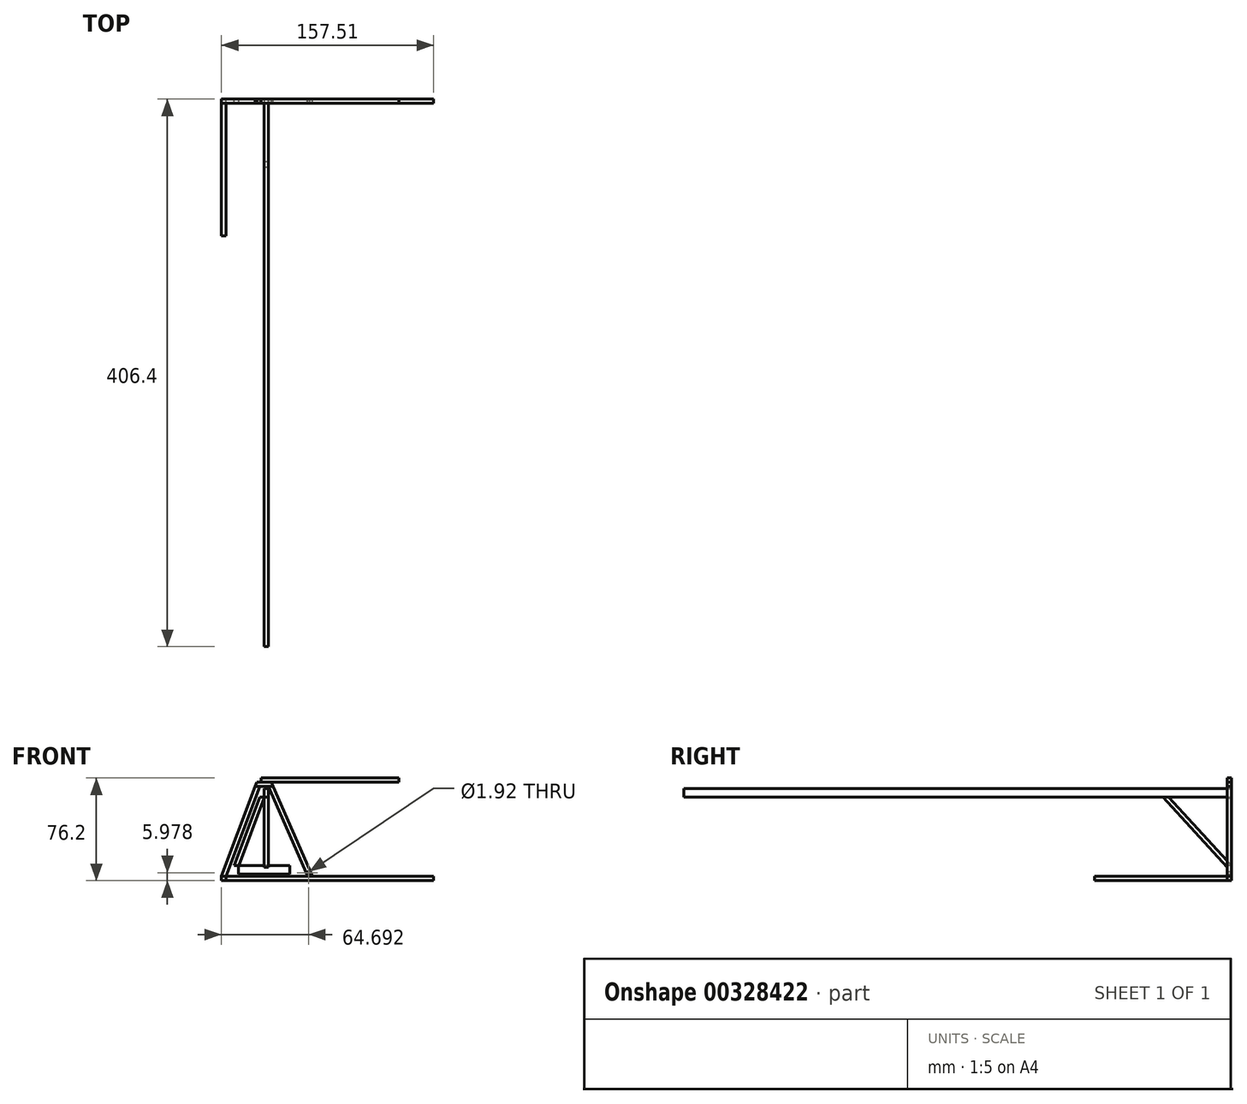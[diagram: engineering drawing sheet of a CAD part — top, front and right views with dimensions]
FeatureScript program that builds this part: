
annotation { "Feature Type Name" : "Feature", "Feature Type Description" : "" }
export const myFeature = defineFeature(function(context is Context, id is Id, definition is map)
    precondition{}
    {
        {
            var Q0;
            Q0=qCreatedBy(makeId("Front.planeOp"),FACE);
            var sketch = newSketch(context, id + "F0", { "sketchPlane" : qUnion([Q0])});
            skLineSegment(sketch, "E0", {"start": v(-19.05, 0) * mm, "end": v(19.05, 0) * mm});
            skLineSegment(sketch, "E1", {"start": v(19.05, 0) * mm, "end": v(19.05, 6.35) * mm});
            skLineSegment(sketch, "E2", {"start": v(19.05, 6.35) * mm, "end": v(-19.05, 6.35) * mm});
            skLineSegment(sketch, "E3", {"start": v(-19.05, 6.35) * mm, "end": v(-19.05, 0) * mm});
            skLineSegment(sketch, "E4", {"start": v(19.05, 6.35) * mm, "end": v(22.23, 6.35) * mm});
            skLineSegment(sketch, "E5", {"start": v(22.23, 6.35) * mm, "end": v(22.23, 0) * mm});
            skLineSegment(sketch, "E6", {"start": v(22.23, 0) * mm, "end": v(19.05, 0) * mm});
            skLineSegment(sketch, "E7", {"start": v(-19.05, 0) * mm, "end": v(-22.23, 0) * mm});
            skLineSegment(sketch, "E8", {"start": v(-22.23, 0) * mm, "end": v(-22.23, 6.35) * mm});
            skLineSegment(sketch, "E9", {"start": v(-22.23, 6.35) * mm, "end": v(-19.05, 6.35) * mm});
            skLineSegment(sketch, "E10", {"start": v(-22.23, 6.35) * mm, "end": v(-3.17, 57.15) * mm});
            skLineSegment(sketch, "E11", {"start": v(-3.18, 57.15) * mm, "end": v(0, 57.15) * mm});
            skLineSegment(sketch, "E12", {"start": v(3.17, 57.15) * mm, "end": v(22.23, 6.35) * mm});
            skLineSegment(sketch, "E13", {"start": v(0, 57.15) * mm, "end": v(3.17, 57.15) * mm});
            skLineSegment(sketch, "E14", {"start": v(-3.18, 57.15) * mm, "end": v(-3.18, 63.5) * mm});
            skLineSegment(sketch, "E15", {"start": v(-3.18, 63.5) * mm, "end": v(0, 63.5) * mm});
            skLineSegment(sketch, "E16", {"start": v(0, 63.5) * mm, "end": v(0, 57.15) * mm});
            skLineSegment(sketch, "E17", {"start": v(3.17, 57.15) * mm, "end": v(3.17, 63.5) * mm});
            skLineSegment(sketch, "E18", {"start": v(0, 63.5) * mm, "end": v(3.17, 63.5) * mm});
            skLineSegment(sketch, "E19", {"start": v(0, 56.57) * mm, "end": v(-18.83, 6.35) * mm});
            skLineSegment(sketch, "E20", {"start": v(0, 57.15) * mm, "end": v(0, 6.35) * mm, "construction": true});
            skLineSegment(sketch, "E21.MirrorCS", {"start": v(0, 56.57) * mm, "end": v(18.83, 6.35) * mm});
            skLineSegment(sketch, "E22", {"start": v(0, 57.15) * mm, "end": v(0, 56.57) * mm});
            skSolve(sketch);
        }
        {
            var Q0;
            Q0=makeQuery(id+"F0.imprint","IMPRINT",FACE,{"disambiguationData":[TD([[makeQuery(id+"F0.imprint","IMPRINT",EDGE,{"derivedFrom":sQuery(id+"F0.wireOp",EDGE,"E13")}),1.0]])]});
            extrude(context, id + "F1", {"entities" : qUnion([Q0]), "depth" : 406.4 * mm});
        }
        {
            var Q0;
            {var subQ1=sQuery(id+"F0.wireOp",EDGE,"E9");Q0=makeQuery(id+"F0.imprint","IMPRINT",FACE,{"disambiguationData":[TD([[makeQuery(id+"F0.imprint","IMPRINT",EDGE,{"derivedFrom":subQ1}),1.0]])]});}
            extrude(context, id + "F2", {"entities" : qUnion([Q0]), "depth" : 3.17 * mm});
        }
        {
            var Q0;
            Q0=makeQuery(id+"F0.imprint","IMPRINT",FACE,{"disambiguationData":[TD([[makeQuery(id+"F0.imprint","IMPRINT",EDGE,{"derivedFrom":sQuery(id+"F0.wireOp",EDGE,"E0")}),1.0]])]});
            extrude(context, id + "F3", {"entities" : qUnion([Q0]), "depth" : 1 / 203.2 * mm});
        }
        {
            var Q0;
            Q0=qCreatedBy(makeId("Right.planeOp"),FACE);
            var sketch = newSketch(context, id + "F4", { "sketchPlane" : qUnion([Q0])});
            skLineSegment(sketch, "E23.0.1", {"start": v(0, 6.35) * mm, "end": v(-3.18, 6.35) * mm});
            skLineSegment(sketch, "E23.0.3", {"start": v(-3.18, 6.35) * mm, "end": v(0, 6.35) * mm});
            skLineSegment(sketch, "E24.0.1", {"start": v(0, 57.15) * mm, "end": v(-406.4, 57.15) * mm});
            skLineSegment(sketch, "E24.0.3", {"start": v(-406.4, 57.15) * mm, "end": v(0, 57.15) * mm});
            skLineSegment(sketch, "E25", {"start": v(0, 6.35) * mm, "end": v(-46.5, 57.15) * mm});
            skLineSegment(sketch, "E26.0", {"start": v(-0.15, 1.81) * mm, "end": v(-50.8, 57.15) * mm});
            skLineSegment(sketch, "E27.0.1", {"start": v(-3.18, 6.35) * mm, "end": v(-3.18, 0) * mm});
            skLineSegment(sketch, "E27.0.3", {"start": v(-3.18, 0) * mm, "end": v(-3.18, 6.35) * mm});
            skSolve(sketch);
        }
        {
            var Q0;
            Q0 = qSketchRegion(id + "F4", true);
            extrude(context, id + "F5", {"entities" : qUnion([Q0]), "depth" : 3.17 * mm});
        }
        {
            var Q0;
            Q0=makeQuery(id+"F3.opExtrude","CAP_FACE",FACE,{"disambiguationData":[OSD([sQuery(id+"F0.wireOp",EDGE,"E0"),sQuery(id+"F0.wireOp",EDGE,"E1"),sQuery(id+"F0.wireOp",EDGE,"E2"),sQuery(id+"F0.wireOp",EDGE,"E3")])],"isStart":true});
            var sketch = newSketch(context, id + "F6", { "sketchPlane" : qUnion([Q0])});
            skLineSegment(sketch, "E28", {"start": v(-3.26, 64.88) * mm, "end": v(-32.43, -1.8) * mm});
            skLineSegment(sketch, "E29", {"start": v(-32.43, -1.8) * mm, "end": v(28.34, -1.8) * mm});
            skLineSegment(sketch, "E30", {"start": v(28.34, -1.8) * mm, "end": v(3.34, 64.88) * mm});
            skLineSegment(sketch, "E31", {"start": v(28.34, -1.8) * mm, "end": v(28.34, -4.97) * mm});
            skLineSegment(sketch, "E32", {"start": v(28.34, -4.97) * mm, "end": v(-125.78, -4.97) * mm});
            skLineSegment(sketch, "E33", {"start": v(-125.78, -1.8) * mm, "end": v(-32.43, -1.8) * mm});
            skLineSegment(sketch, "E34", {"start": v(-125.78, -1.8) * mm, "end": v(-125.78, -4.97) * mm});
            skLineSegment(sketch, "E35", {"start": v(6.73, 64.88) * mm, "end": v(-6.73, 64.88) * mm});
            skLineSegment(sketch, "E36.0", {"start": v(-5.34, 68.05) * mm, "end": v(-35.9, -1.8) * mm});
            skLineSegment(sketch, "E36.1", {"start": v(31.73, -1.8) * mm, "end": v(5.54, 68.05) * mm});
            skLineSegment(sketch, "E37", {"start": v(28.34, -1.8) * mm, "end": v(31.73, -1.8) * mm});
            skLineSegment(sketch, "E38", {"start": v(31.73, -4.97) * mm, "end": v(28.34, -4.97) * mm});
            skLineSegment(sketch, "E39", {"start": v(31.73, -4.97) * mm, "end": v(31.73, -1.8) * mm});
            skPoint(sketch, "E40", {"position": v(-48.72, -4.97) * mm});
            skLineSegment(sketch, "E41", {"start": v(-5.34, 68.05) * mm, "end": v(5.54, 68.05) * mm});
            skLineSegment(sketch, "E42.bottom", {"start": v(2.36, 68.05) * mm, "end": v(-99.8, 68.05) * mm});
            skLineSegment(sketch, "E42.top", {"start": v(2.36, 71.23) * mm, "end": v(-99.8, 71.23) * mm});
            skLineSegment(sketch, "E42.left", {"start": v(2.36, 68.05) * mm, "end": v(2.36, 71.23) * mm});
            skLineSegment(sketch, "E42.right", {"start": v(-99.8, 68.05) * mm, "end": v(-99.8, 71.23) * mm});
            skLineSegment(sketch, "E43", {"start": v(-48.72, -4.97) * mm, "end": v(-48.72, 68.05) * mm, "construction": true});
            skPoint(sketch, "E44.0", {"position": v(-1.59, 57.15) * mm});
            skPoint(sketch, "E45.0", {"position": v(0, 57.15) * mm});
            skLineSegment(sketch, "E46", {"start": v(0, 57.15) * mm, "end": v(-22.23, 6.35) * mm, "construction": true});
            skPoint(sketch, "E47.0", {"position": v(22.23, 6.35) * mm});
            skPoint(sketch, "E48.orphan", {"position": v(-1.88, 68.05) * mm});
            skPoint(sketch, "E49.orphan", {"position": v(2.15, 68.05) * mm});
            skLineSegment(sketch, "E50", {"start": v(0, 57.15) * mm, "end": v(0, 64.88) * mm, "construction": true});
            skLineSegment(sketch, "E51", {"start": v(-22.22, 6.35) * mm, "end": v(22.23, 6.35) * mm, "construction": true});
            skLineSegment(sketch, "E52", {"start": v(0, 57.15) * mm, "end": v(0, 6.35) * mm, "construction": true});
            skCircle(sketch, "E53", {"center": v(-32.96, 1) * mm, "radius": 0.96 * mm});
            skSolve(sketch);
        }
        {
            var Q0;
            {var subQ3=sQuery(id+"F6.wireOp",EDGE,"E29");Q0=makeQuery(id+"F6.imprint","IMPRINT",FACE,{"disambiguationData":[TD([[makeQuery(id+"F6.imprint","IMPRINT",EDGE,{"derivedFrom":subQ3}),-1.0]])]});}
            extrude(context, id + "F7", {"entities" : qUnion([Q0]), "oppositeDirection" : true, "depth" : 3.17 * mm});
        }
        {
            var Q0;
            {var subQ0=sQuery(id+"F6.wireOp",EDGE,"E36.1");Q0=makeQuery(id+"F6.imprint","IMPRINT",FACE,{"disambiguationData":[TD([[makeQuery(id+"F6.imprint","IMPRINT",EDGE,{"derivedFrom":subQ0}),1.0]])]});}
            extrude(context, id + "F8", {"entities" : qUnion([Q0]), "oppositeDirection" : true, "depth" : 3.17 * mm});
        }
        {
            var Q0;
            {var subQ3=sQuery(id+"F6.wireOp",EDGE,"E36.0");Q0=makeQuery(id+"F6.imprint","IMPRINT",FACE,{"disambiguationData":[TD([[makeQuery(id+"F6.imprint","IMPRINT",EDGE,{"derivedFrom":subQ3}),1.0]])]});}
            extrude(context, id + "F9", {"entities" : qUnion([Q0]), "oppositeDirection" : true, "depth" : 3.17 * mm});
        }
        {
            var Q0;
            Q0=makeQuery(id+"F6.imprint","IMPRINT",FACE,{"disambiguationData":[TD([[makeQuery(id+"F6.imprint","IMPRINT",EDGE,{"derivedFrom":sQuery(id+"F6.wireOp",EDGE,"E42.top")}),1.0]])]});
            extrude(context, id + "F10", {"entities" : qUnion([Q0]), "oppositeDirection" : true, "depth" : 3.17 * mm});
        }
        {
            var Q0;
            {var subQ3=sQuery(id+"F6.wireOp",EDGE,"E35");Q0=makeQuery(id+"F6.imprint","IMPRINT",FACE,{"disambiguationData":[TD([[makeQuery(id+"F6.imprint","IMPRINT",EDGE,{"derivedFrom":subQ3}),-1.0]])]});}
            extrude(context, id + "F11", {"entities" : qUnion([Q0]), "oppositeDirection" : true, "depth" : 3.17 * mm});
        }
        {
            var Q0;
            Q0=makeQuery(id+"F6.imprint","IMPRINT",FACE,{"disambiguationData":[TD([[makeQuery(id+"F6.imprint","IMPRINT",EDGE,{"derivedFrom":sQuery(id+"F6.wireOp",EDGE,"E31")}),1.0]])]});
            extrude(context, id + "F12", {"entities" : qUnion([Q0]), "oppositeDirection" : true, "depth" : 101.6 * mm});
        }
    });
